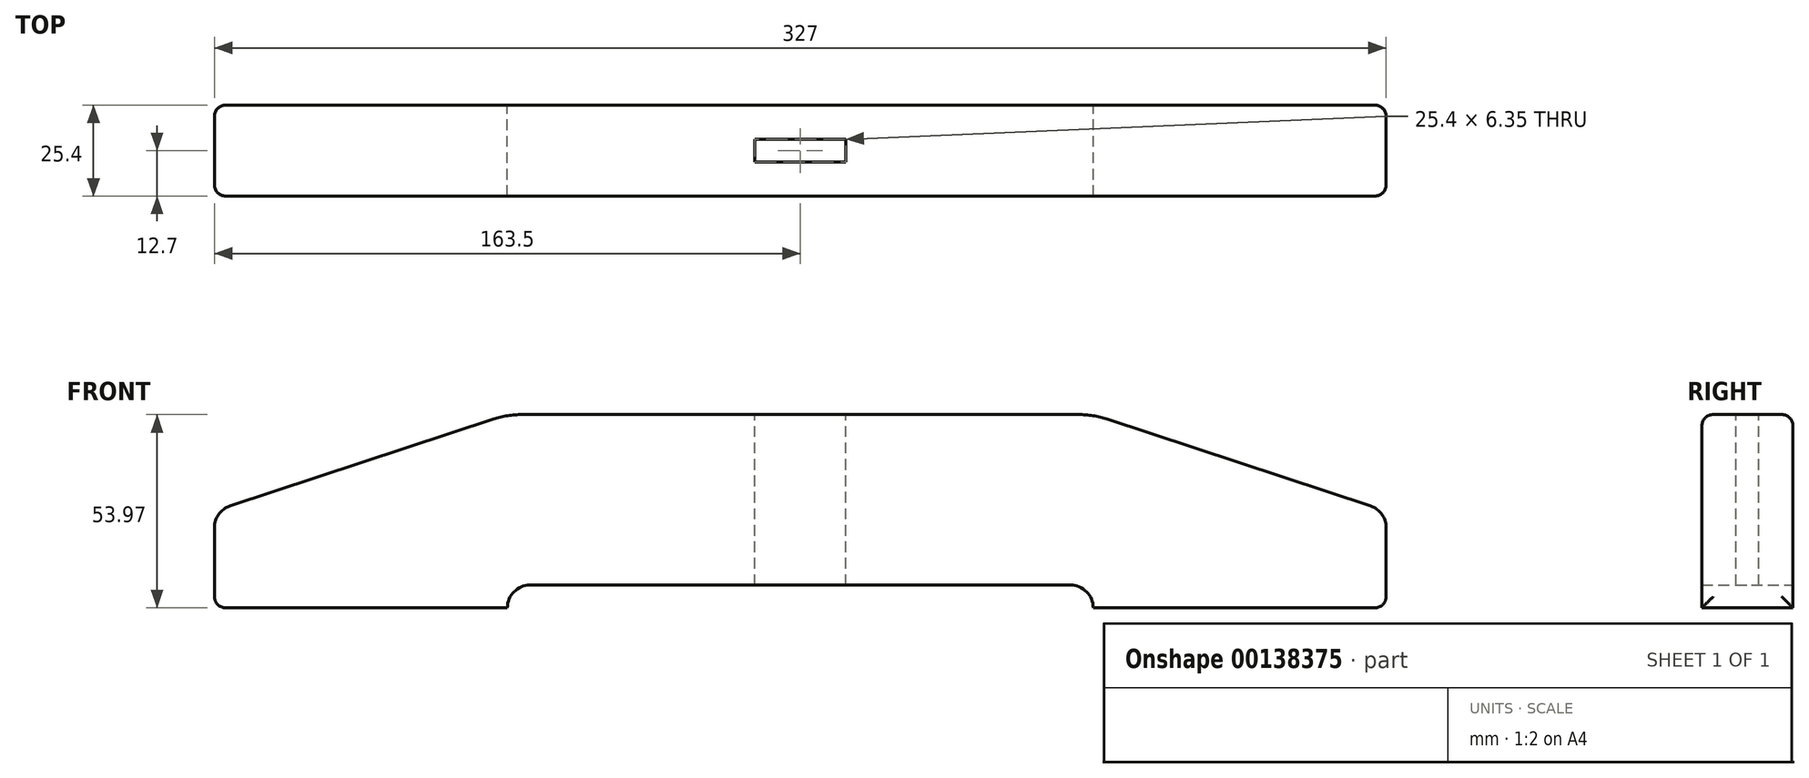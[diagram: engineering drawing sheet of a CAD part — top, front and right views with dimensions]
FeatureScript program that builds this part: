
annotation { "Feature Type Name" : "Feature", "Feature Type Description" : "" }
export const myFeature = defineFeature(function(context is Context, id is Id, definition is map)
    precondition{}
    {
        {
            var Q0;
            Q0=qCreatedBy(makeId("Front.planeOp"),FACE);
            var sketch = newSketch(context, id + "F0", { "sketchPlane" : qUnion([Q0])});
            skPoint(sketch, "E0.middle", {"position": v(0, 0) * mm});
            skLineSegment(sketch, "E1", {"start": v(-159.14, 1.44) * mm, "end": v(-85.62, 25.71) * mm});
            skLineSegment(sketch, "E2", {"start": v(-163.5, -4.6) * mm, "end": v(-163.5, -26.98) * mm});
            skLineSegment(sketch, "E3", {"start": v(-81.74, -26.98) * mm, "end": v(-81.74, -26.98) * mm});
            skLineSegment(sketch, "E4", {"start": v(-75.4, -20.63) * mm, "end": v(0, -20.63) * mm});
            skLineSegment(sketch, "E5", {"start": v(-77.65, 27) * mm, "end": v(0, 27) * mm});
            skLineSegment(sketch, "E6", {"start": v(-163.5, -26.98) * mm, "end": v(-81.74, -26.98) * mm});
            skPoint(sketch, "E7.visualSharp", {"position": v(-81.74, -20.63) * mm});
            skArc(sketch, "E7.filletArc", {"start": v(-75.4, -20.63) * mm, "mid": v(-79.88, -22.5) * mm, "end": v(-81.74, -26.98) * mm});
            skPoint(sketch, "E8.visualSharp", {"position": v(-163.5, 0) * mm});
            skArc(sketch, "E8.filletArc", {"start": v(-159.14, 1.44) * mm, "mid": v(-162.3, -0.87) * mm, "end": v(-163.5, -4.6) * mm});
            skPoint(sketch, "E9.visualSharp", {"position": v(-81.74, 27) * mm});
            skArc(sketch, "E9.filletArc", {"start": v(-77.65, 27) * mm, "mid": v(-81.69, 26.67) * mm, "end": v(-85.62, 25.71) * mm});
            skLineSegment(sketch, "E10.MirrorCS", {"start": v(75.4, -20.63) * mm, "end": v(0, -20.63) * mm});
            skArc(sketch, "E11.MirrorCS", {"start": v(75.4, -20.63) * mm, "mid": v(79.88, -22.5) * mm, "end": v(81.74, -26.98) * mm});
            skLineSegment(sketch, "E12.MirrorCS", {"start": v(163.5, -26.98) * mm, "end": v(81.74, -26.98) * mm});
            skLineSegment(sketch, "E13.MirrorCS", {"start": v(163.5, -4.6) * mm, "end": v(163.5, -26.98) * mm});
            skArc(sketch, "E14.MirrorCS", {"start": v(159.14, 1.44) * mm, "mid": v(162.3, -0.87) * mm, "end": v(163.5, -4.6) * mm});
            skLineSegment(sketch, "E15.MirrorCS", {"start": v(159.14, 1.44) * mm, "end": v(85.62, 25.71) * mm});
            skArc(sketch, "E16.MirrorCS", {"start": v(77.65, 27) * mm, "mid": v(81.69, 26.67) * mm, "end": v(85.62, 25.71) * mm});
            skLineSegment(sketch, "E17.MirrorCS", {"start": v(77.65, 27) * mm, "end": v(0, 27) * mm});
            skSolve(sketch);
        }
        {
            var Q0;
            Q0=makeQuery(id+"F0.imprint","IMPRINT",FACE,{"disambiguationData":[TD([[makeQuery(id+"F0.imprint","IMPRINT",EDGE,{"derivedFrom":sQuery(id+"F0.wireOp",EDGE,"E1")}),-1.0]])]});
            extrude(context, id + "F1", {"entities" : qUnion([Q0]), "depth" : 25.4 * mm});
        }
        {
            var Q0;
            Q0=makeQuery(id+"F1.opExtrude","CAP_EDGE",EDGE,{"disambiguationData":[OSD([sQuery(id+"F0.wireOp",EDGE,"E2")])],"isStart":false});
            var Q1;
            Q1=makeQuery(id+"F1.opExtrude","CAP_EDGE",EDGE,{"disambiguationData":[OSD([sQuery(id+"F0.wireOp",EDGE,"E8.filletArc")])],"isStart":false});
            var Q2;
            Q2=makeQuery(id+"F1.opExtrude","CAP_EDGE",EDGE,{"disambiguationData":[OSD([sQuery(id+"F0.wireOp",EDGE,"E1")])],"isStart":false});
            var Q3;
            Q3=makeQuery(id+"F1.opExtrude","CAP_EDGE",EDGE,{"disambiguationData":[OSD([sQuery(id+"F0.wireOp",EDGE,"E15.MirrorCS")])],"isStart":true});
            var Q4;
            Q4=makeQuery(id+"F1.opExtrude","SWEPT_EDGE",EDGE,{"disambiguationData":[OSD([sQuery(id+"F0.wireOp",EDGE,"E2"),sQuery(id+"F0.wireOp",EDGE,"E6")])]});
            var Q5;
            Q5=makeQuery(id+"F1.opExtrude","SWEPT_EDGE",EDGE,{"disambiguationData":[OSD([sQuery(id+"F0.wireOp",EDGE,"E12.MirrorCS"),sQuery(id+"F0.wireOp",EDGE,"E13.MirrorCS")])]});
            fillet(context, id + "F2", {"entities" : qUnion([Q0, Q1, Q2, Q3, Q4, Q5]), "radius" : 3.17 * mm, "tangentPropagation" : true, "allowEdgeOverflow" : false});
        }
        {
            var Q0;
            Q0=makeQuery(id+"F1.opExtrude","SWEPT_FACE",FACE,{"disambiguationData":[OSD([sQuery(id+"F0.wireOp",EDGE,"E5"),sQuery(id+"F0.wireOp",EDGE,"E17.MirrorCS")])]});
            var sketch = newSketch(context, id + "F3", { "sketchPlane" : qUnion([Q0])});
            skLineSegment(sketch, "E18.bottom", {"start": v(12.7, -15.88) * mm, "end": v(-12.7, -15.88) * mm});
            skLineSegment(sketch, "E18.top", {"start": v(12.7, -9.52) * mm, "end": v(-12.7, -9.52) * mm});
            skLineSegment(sketch, "E18.left", {"start": v(12.7, -15.88) * mm, "end": v(12.7, -9.52) * mm});
            skLineSegment(sketch, "E18.right", {"start": v(-12.7, -15.88) * mm, "end": v(-12.7, -9.52) * mm});
            skPoint(sketch, "E18.middle", {"position": v(0, -12.7) * mm});
            skSolve(sketch);
        }
        {
            var Q0;
            Q0=makeQuery(id+"F3.imprint","IMPRINT",FACE,{"disambiguationData":[TD([[makeQuery(id+"F3.imprint","IMPRINT",EDGE,{"derivedFrom":sQuery(id+"F3.wireOp",EDGE,"E18.bottom")}),-1.0]])]});
            extrude(context, id + "F4", {"entities" : qUnion([Q0]), "operationType" : NewBodyOperationType.REMOVE, "endBound" : BoundingType.THROUGH_ALL, "oppositeDirection" : true, "depth" : 25.4 * mm});
        }
    });
